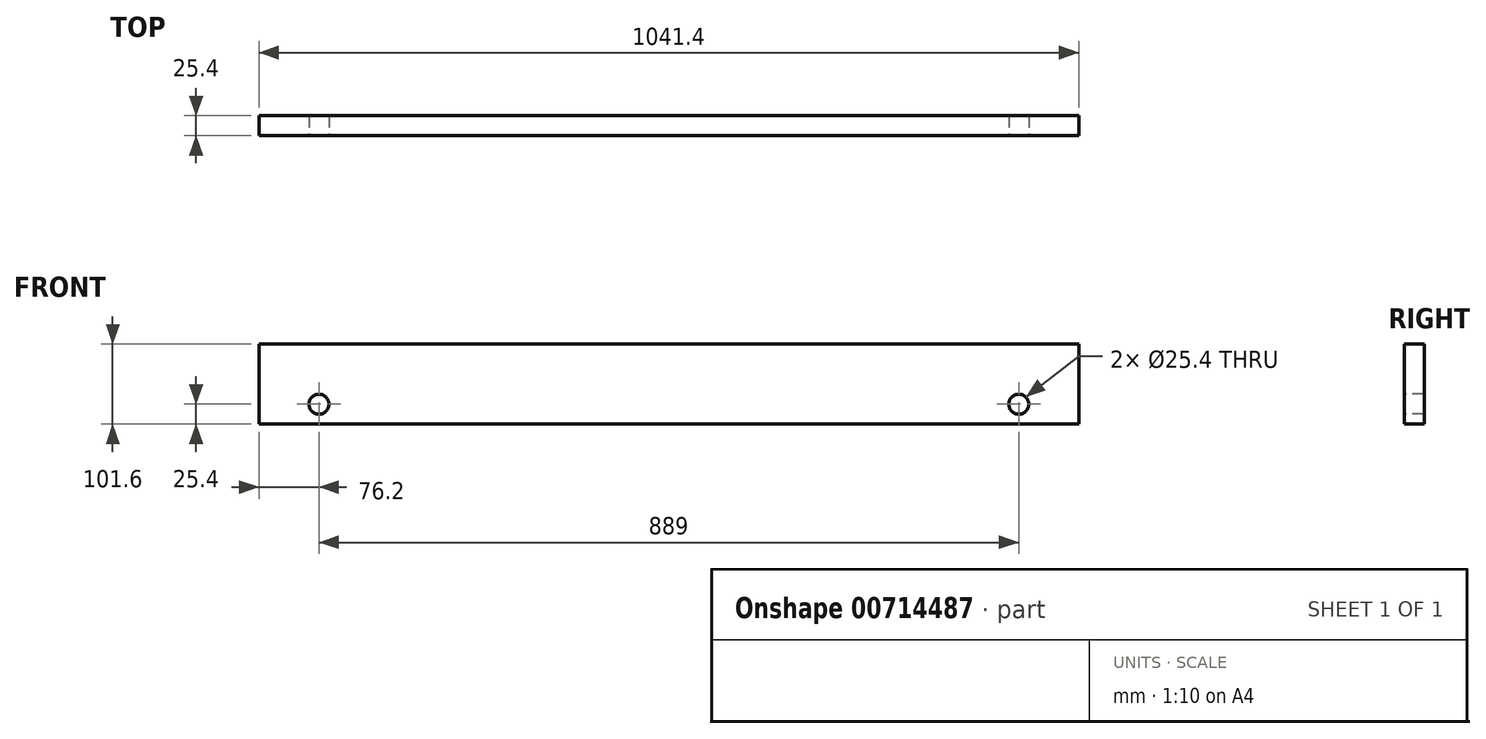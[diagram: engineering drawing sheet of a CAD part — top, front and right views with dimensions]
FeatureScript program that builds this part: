
annotation { "Feature Type Name" : "Feature", "Feature Type Description" : "" }
export const myFeature = defineFeature(function(context is Context, id is Id, definition is map)
    precondition{}
    {
        {
            var Q0;
            Q0=qCreatedBy(makeId("Front.planeOp"),FACE);
            var sketch = newSketch(context, id + "F0", { "sketchPlane" : qUnion([Q0])});
            skLineSegment(sketch, "E0.bottom", {"start": v(0, 101.6) * mm, "end": v(1041.4, 101.6) * mm});
            skLineSegment(sketch, "E0.top", {"start": v(0, 0) * mm, "end": v(1041.4, 0) * mm});
            skLineSegment(sketch, "E0.left", {"start": v(0, 101.6) * mm, "end": v(0, 0) * mm});
            skLineSegment(sketch, "E0.right", {"start": v(1041.4, 101.6) * mm, "end": v(1041.4, 0) * mm});
            skSolve(sketch);
        }
        {
            var Q0;
            Q0=makeQuery(id+"F0.imprint","IMPRINT",FACE,{"disambiguationData":[TD([[makeQuery(id+"F0.imprint","IMPRINT",EDGE,{"derivedFrom":sQuery(id+"F0.wireOp",EDGE,"E0.bottom")}),-1.0]])]});
            extrude(context, id + "F1", {"entities" : qUnion([Q0]), "depth" : 25.4 * mm, "offsetDistance" : 25.4 * mm});
        }
        {
            var Q0;
            Q0=makeQuery(id+"F1.opExtrude","CAP_FACE",FACE,{"disambiguationData":[OSD([sQuery(id+"F0.wireOp",EDGE,"E0.bottom"),sQuery(id+"F0.wireOp",EDGE,"E0.top"),sQuery(id+"F0.wireOp",EDGE,"E0.left"),sQuery(id+"F0.wireOp",EDGE,"E0.right")])],"isStart":false});
            var sketch = newSketch(context, id + "F2", { "sketchPlane" : qUnion([Q0])});
            skLineSegment(sketch, "E1", {"start": v(0, 50.8) * mm, "end": v(76.2, 50.8) * mm, "construction": true});
            skLineSegment(sketch, "E2", {"start": v(1041.4, 50.8) * mm, "end": v(965.2, 50.8) * mm, "construction": true});
            skLineSegment(sketch, "E3", {"start": v(76.2, 101.6) * mm, "end": v(76.2, 50.8) * mm});
            skLineSegment(sketch, "E4", {"start": v(76.2, 50.8) * mm, "end": v(76.2, 0) * mm});
            skPoint(sketch, "E5", {"position": v(76.2, 25.4) * mm});
            skPoint(sketch, "E6", {"position": v(76.2, 76.2) * mm});
            skLineSegment(sketch, "E7", {"start": v(965.2, 101.6) * mm, "end": v(965.2, 50.8) * mm});
            skLineSegment(sketch, "E8", {"start": v(965.2, 50.8) * mm, "end": v(965.2, 0) * mm});
            skPoint(sketch, "E9", {"position": v(965.2, 25.4) * mm});
            skPoint(sketch, "E10", {"position": v(965.2, 76.2) * mm});
            skCircle(sketch, "E11", {"center": v(965.2, 25.4) * mm, "radius": 12.7 * mm});
            skCircle(sketch, "E12", {"center": v(76.2, 25.4) * mm, "radius": 12.7 * mm});
            skSolve(sketch);
        }
        {
            var Q0;
            Q0 = qSketchRegion(id + "F2", true);
            extrude(context, id + "F3", {"entities" : qUnion([Q0]), "operationType" : NewBodyOperationType.REMOVE, "endBound" : BoundingType.THROUGH_ALL, "oppositeDirection" : true, "depth" : 25.4 * mm, "offsetDistance" : 25.4 * mm});
        }
    });
